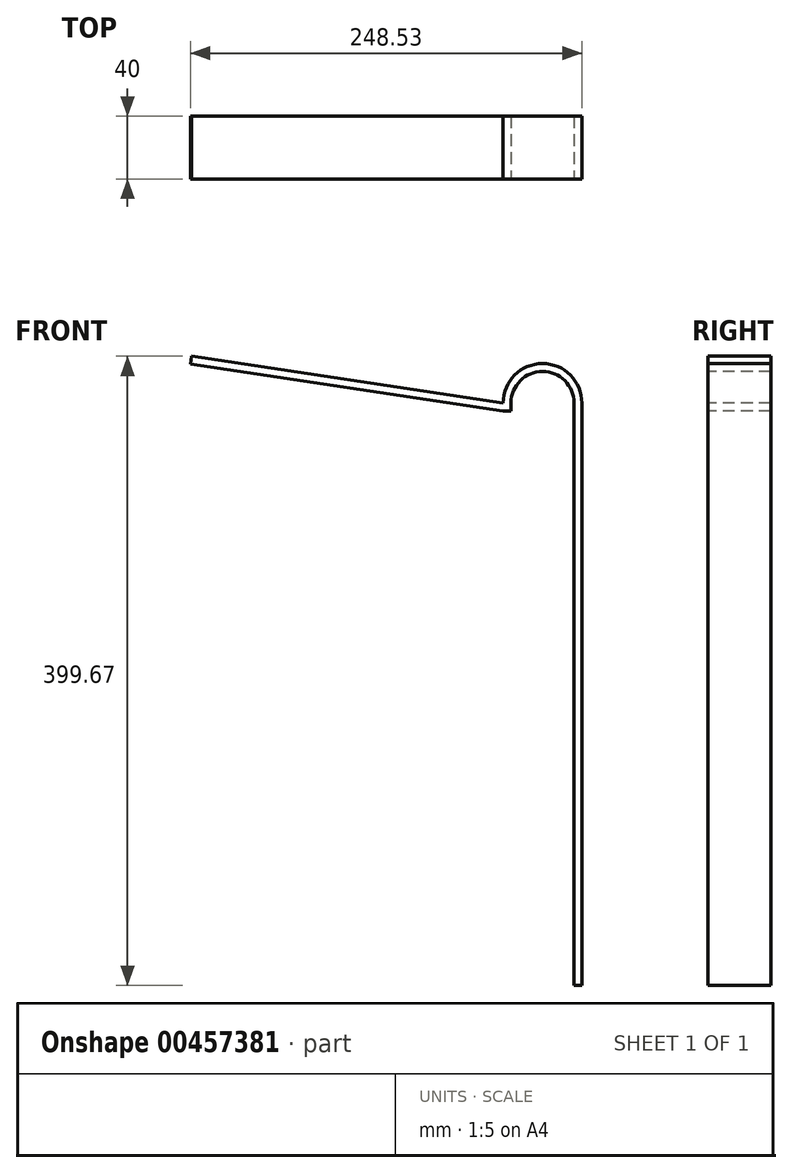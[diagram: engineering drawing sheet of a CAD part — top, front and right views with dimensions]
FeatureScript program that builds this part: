
annotation { "Feature Type Name" : "Feature", "Feature Type Description" : "" }
export const myFeature = defineFeature(function(context is Context, id is Id, definition is map)
    precondition{}
    {
        {
            var Q0;
            Q0=qCreatedBy(makeId("Front.planeOp"),FACE);
            var sketch = newSketch(context, id + "F0", { "sketchPlane" : qUnion([Q0])});
            skLineSegment(sketch, "E0", {"start": v(0, 0) * mm, "end": v(0, 370) * mm});
            skArc(sketch, "E1", {"start": v(0, 370) * mm, "mid": v(-25, 395) * mm, "end": v(-50, 370) * mm});
            skLineSegment(sketch, "E2", {"start": v(-247.79, 399.67) * mm, "end": v(-50, 370) * mm});
            skLineSegment(sketch, "E3.0", {"start": v(-248.53, 394.72) * mm, "end": v(-50, 364.94) * mm});
            skArc(sketch, "E4.0", {"start": v(-5, 370) * mm, "mid": v(-25, 390) * mm, "end": v(-45, 370) * mm});
            skLineSegment(sketch, "E5.0", {"start": v(-5, 0) * mm, "end": v(-5, 370) * mm});
            skLineSegment(sketch, "E6", {"start": v(-5, 0) * mm, "end": v(0, 0) * mm});
            skLineSegment(sketch, "E7", {"start": v(-50, 364.94) * mm, "end": v(-45, 364.94) * mm});
            skLineSegment(sketch, "E8", {"start": v(-45, 364.94) * mm, "end": v(-45, 370) * mm});
            skLineSegment(sketch, "E9", {"start": v(-247.79, 399.67) * mm, "end": v(-248.53, 394.72) * mm});
            skSolve(sketch);
        }
        {
            var Q0;
            Q0=makeQuery(id+"F0.imprint","IMPRINT",FACE,{"disambiguationData":[TD([[makeQuery(id+"F0.imprint","IMPRINT",EDGE,{"derivedFrom":sQuery(id+"F0.wireOp",EDGE,"E0")}),1.0]])]});
            extrude(context, id + "F1", {"entities" : qUnion([Q0]), "oppositeDirection" : true, "depth" : 40 * mm});
        }
    });
